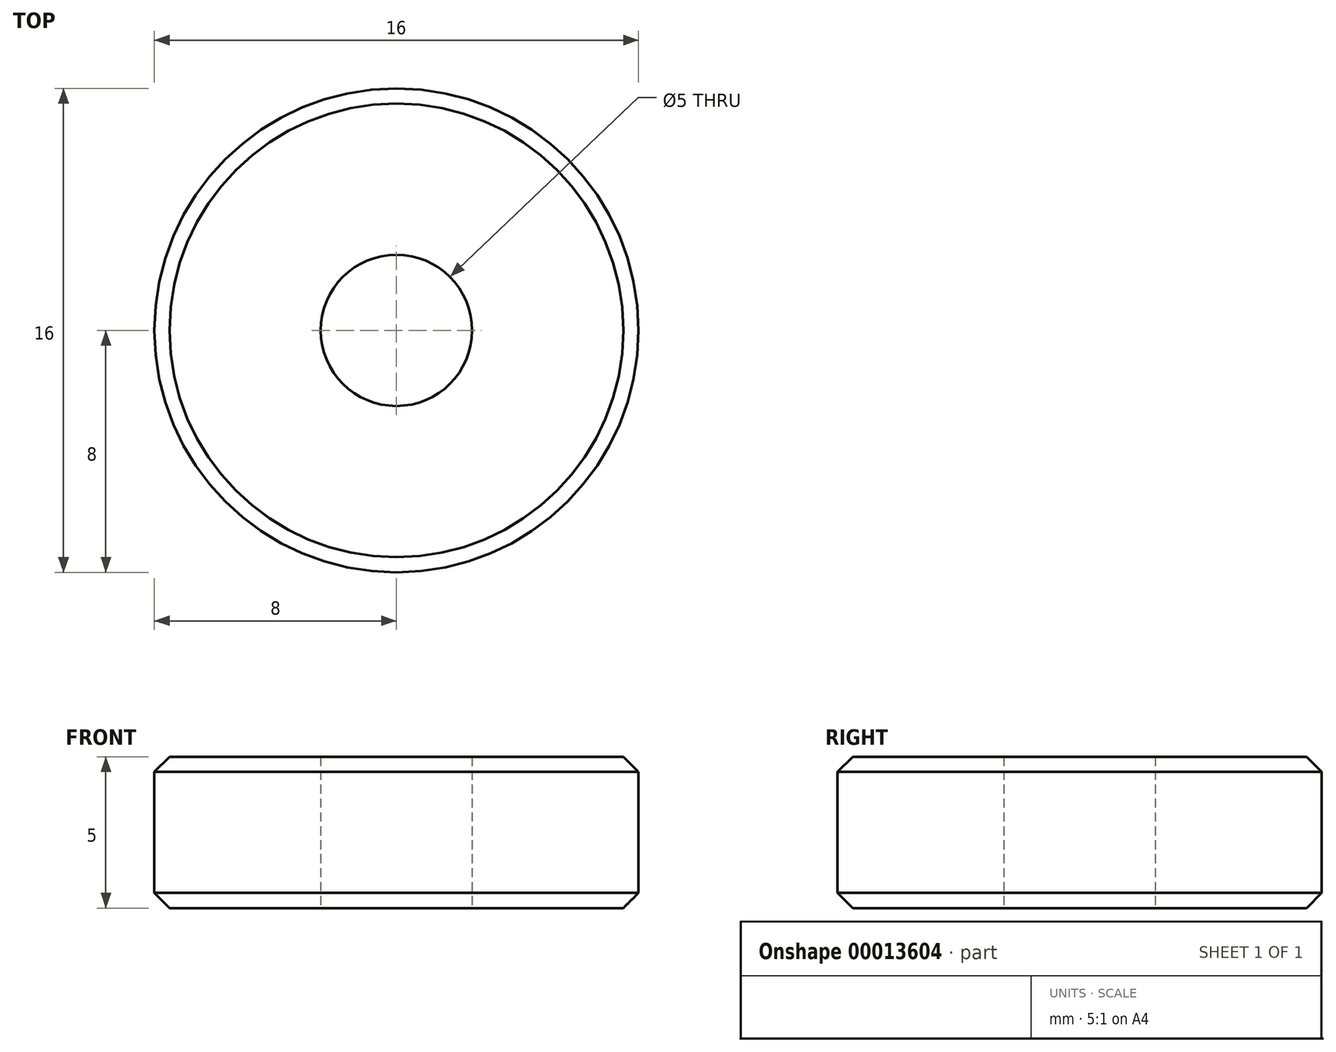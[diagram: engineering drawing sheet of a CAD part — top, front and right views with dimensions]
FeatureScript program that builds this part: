
annotation { "Feature Type Name" : "Feature", "Feature Type Description" : "" }
export const myFeature = defineFeature(function(context is Context, id is Id, definition is map)
    precondition{}
    {
        {
            var Q0;
            Q0=qCreatedBy(makeId("Top.planeOp"),FACE);
            var sketch = newSketch(context, id + "F0", { "sketchPlane" : qUnion([Q0])});
            skCircle(sketch, "E0", {"center": v(0, 0) * mm, "radius": 8 * mm});
            skCircle(sketch, "E1", {"center": v(0, 0) * mm, "radius": 2.5 * mm});
            skSolve(sketch);
        }
        {
            var Q0;
            Q0=makeQuery(id+"F0.imprint","IMPRINT",FACE,{"disambiguationData":[TD([[makeQuery(id+"F0.imprint","IMPRINT",EDGE,{"derivedFrom":sQuery(id+"F0.wireOp",EDGE,"E0")}),1.0]])]});
            extrude(context, id + "F1", {"entities" : qUnion([Q0]), "depth" : 5 * mm});
        }
        {
            var Q0;
            Q0=makeQuery(id+"F1.opExtrude","CAP_EDGE",EDGE,{"disambiguationData":[OSD([sQuery(id+"F0.wireOp",EDGE,"E0")])],"isStart":false});
            var Q1;
            Q1=makeQuery(id+"F1.opExtrude","CAP_EDGE",EDGE,{"disambiguationData":[OSD([sQuery(id+"F0.wireOp",EDGE,"E0")])],"isStart":true});
            chamfer(context, id + "F2", {"entities" : qUnion([Q0, Q1]), "width" : 0.5 * mm, "tangentPropagation" : true});
        }
    });
